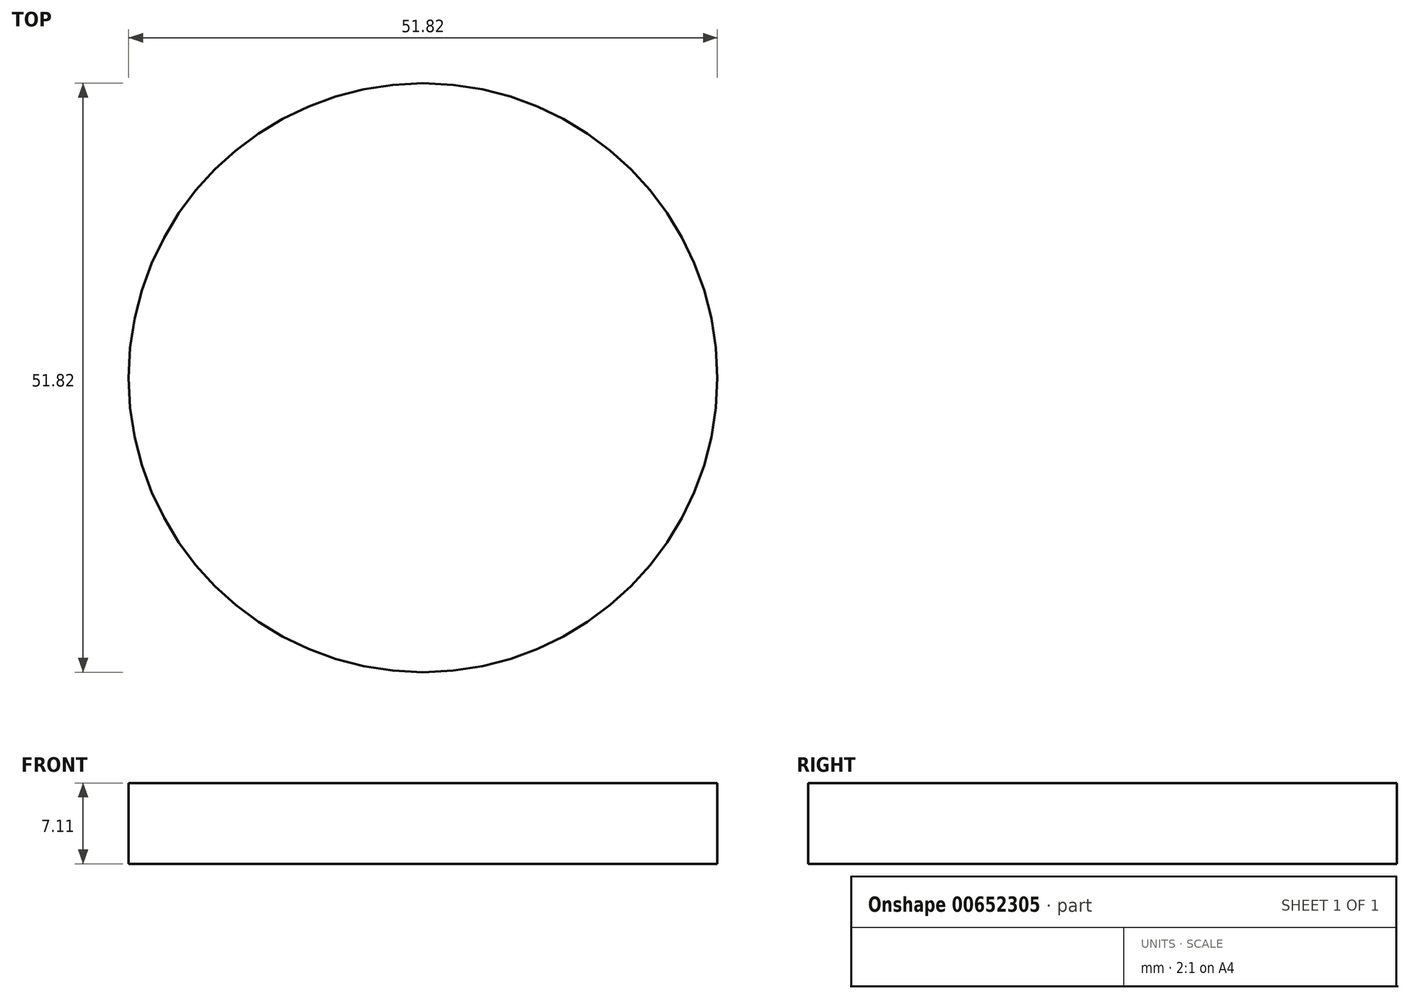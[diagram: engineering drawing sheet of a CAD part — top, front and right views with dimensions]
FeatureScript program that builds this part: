
annotation { "Feature Type Name" : "Feature", "Feature Type Description" : "" }
export const myFeature = defineFeature(function(context is Context, id is Id, definition is map)
    precondition{}
    {
        {
            var Q0;
            Q0=qCreatedBy(makeId("Top.planeOp"),FACE);
            var sketch = newSketch(context, id + "F0", { "sketchPlane" : qUnion([Q0])});
            skCircle(sketch, "E0", {"center": v(0, 0) * mm, "radius": 25.91 * mm});
            skSolve(sketch);
        }
        {
            var Q0;
            Q0=sQuery(id+"F0.wireOp",EDGE,"E0");
            extrude(context, id + "F1", {"bodyType" : ToolBodyType.SURFACE, "surfaceEntities" : qUnion([Q0]), "depth" : 7.11 * mm, "offsetDistance" : 25.4 * mm});
        }
    });
